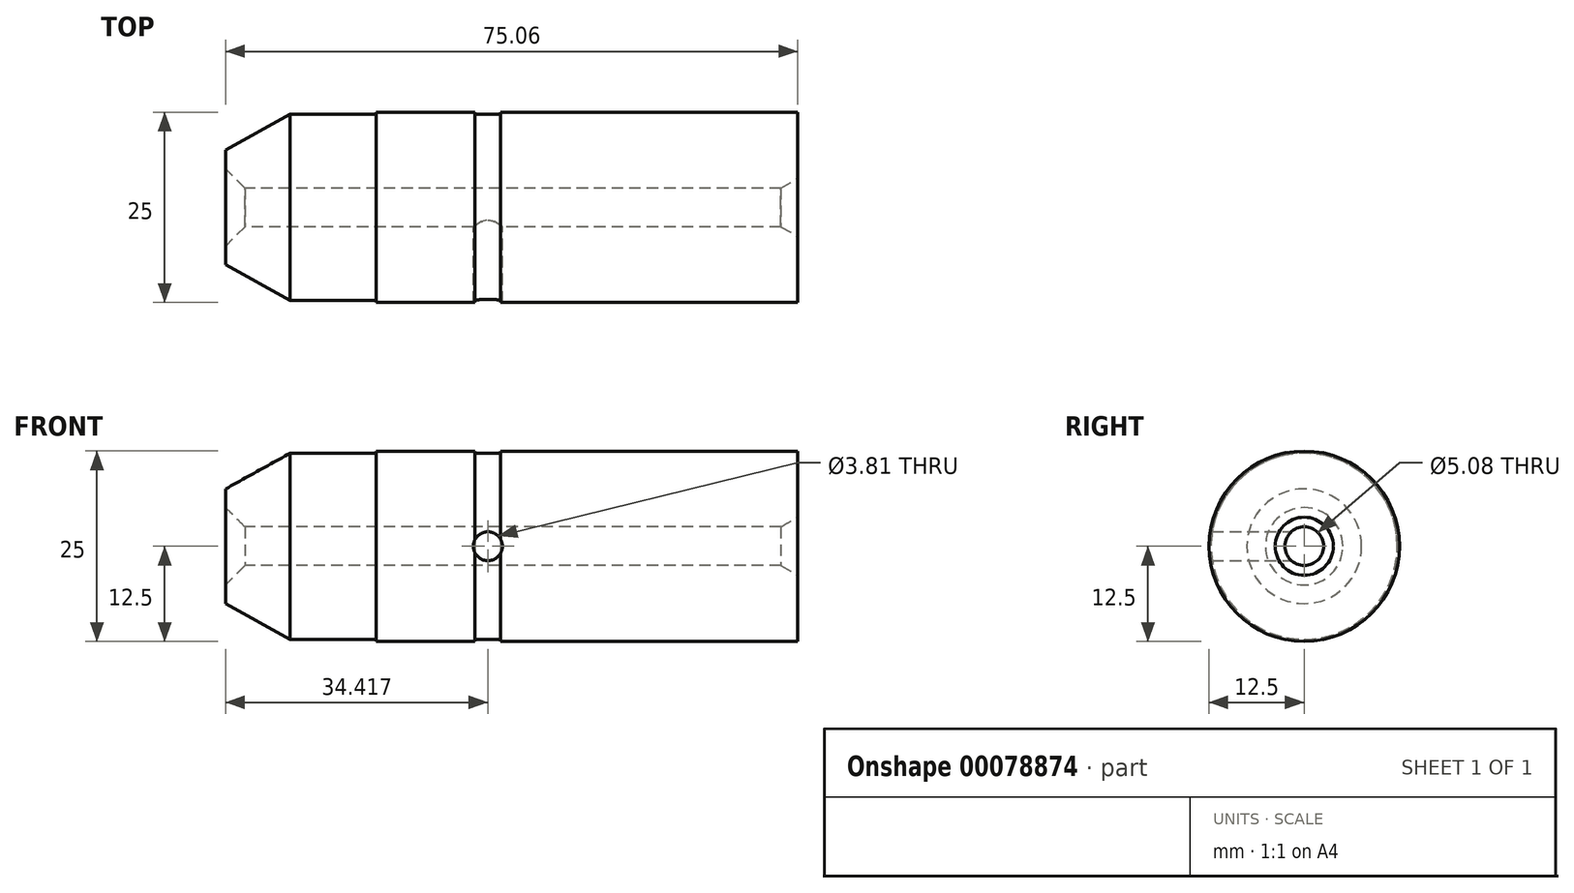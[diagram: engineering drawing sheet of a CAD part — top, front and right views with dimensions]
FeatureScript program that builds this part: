
annotation { "Feature Type Name" : "Feature", "Feature Type Description" : "" }
export const myFeature = defineFeature(function(context is Context, id is Id, definition is map)
    precondition{}
    {
        {
            var Q0;
            Q0=qCreatedBy(makeId("Front.planeOp"),FACE);
            var sketch = newSketch(context, id + "F0", { "sketchPlane" : qUnion([Q0])});
            skLineSegment(sketch, "E0", {"start": v(-35, 5.08) * mm, "end": v(-35, 7.53) * mm});
            skLineSegment(sketch, "E1", {"start": v(-35, 7.53) * mm, "end": v(-26.54, 12.22) * mm});
            skLineSegment(sketch, "E2", {"start": v(-26.54, 12.22) * mm, "end": v(-15.27, 12.22) * mm});
            skLineSegment(sketch, "E3", {"start": v(-15.27, 12.22) * mm, "end": v(-15.27, 12.5) * mm});
            skLineSegment(sketch, "E4", {"start": v(-15.27, 12.5) * mm, "end": v(-2.27, 12.5) * mm});
            skLineSegment(sketch, "E5", {"start": v(-2.27, 12.5) * mm, "end": v(-2.27, 12.22) * mm});
            skLineSegment(sketch, "E6", {"start": v(-2.27, 12.22) * mm, "end": v(1.08, 12.22) * mm});
            skLineSegment(sketch, "E7", {"start": v(1.08, 12.22) * mm, "end": v(1.08, 12.5) * mm});
            skLineSegment(sketch, "E8", {"start": v(1.08, 12.5) * mm, "end": v(40.05, 12.5) * mm});
            skLineSegment(sketch, "E9", {"start": v(-35, 5.08) * mm, "end": v(-32.47, 2.54) * mm});
            skLineSegment(sketch, "E10", {"start": v(-32.47, 2.54) * mm, "end": v(37.85, 2.54) * mm});
            skLineSegment(sketch, "E11", {"start": v(40.05, 12.5) * mm, "end": v(40.05, 3.81) * mm});
            skLineSegment(sketch, "E12", {"start": v(37.85, 2.54) * mm, "end": v(40.05, 3.81) * mm});
            skLineSegment(sketch, "E13", {"start": v(-68.1, 0) * mm, "end": v(64.32, 0) * mm, "construction": true});
            skSolve(sketch);
        }
        {
            var Q0;
            Q0=makeQuery(id+"F0.imprint","IMPRINT",FACE,{"disambiguationData":[TD([[makeQuery(id+"F0.imprint","IMPRINT",EDGE,{"derivedFrom":sQuery(id+"F0.wireOp",EDGE,"E0")}),-1.0]])]});
            var Q1;
            Q1=sQuery(id+"F0.wireOp",EDGE,"E13");
            revolve(context, id + "F1", {"entities" : qUnion([Q0]), "axis" : qUnion([Q1]), "revolveType" : RevolveType.FULL});
        }
        {
            var Q0;
            Q0=qCreatedBy(makeId("Front.planeOp"),FACE);
            var sketch = newSketch(context, id + "F2", { "sketchPlane" : qUnion([Q0])});
            skCircle(sketch, "E14", {"center": v(-0.6, 0) * mm, "radius": 1.9 * mm});
            skSolve(sketch);
        }
        {
            var Q0;
            Q0 = qSketchRegion(id + "F2", true);
            extrude(context, id + "F3", {"entities" : qUnion([Q0]), "operationType" : NewBodyOperationType.REMOVE, "depth" : 25.4 * mm});
        }
    });
